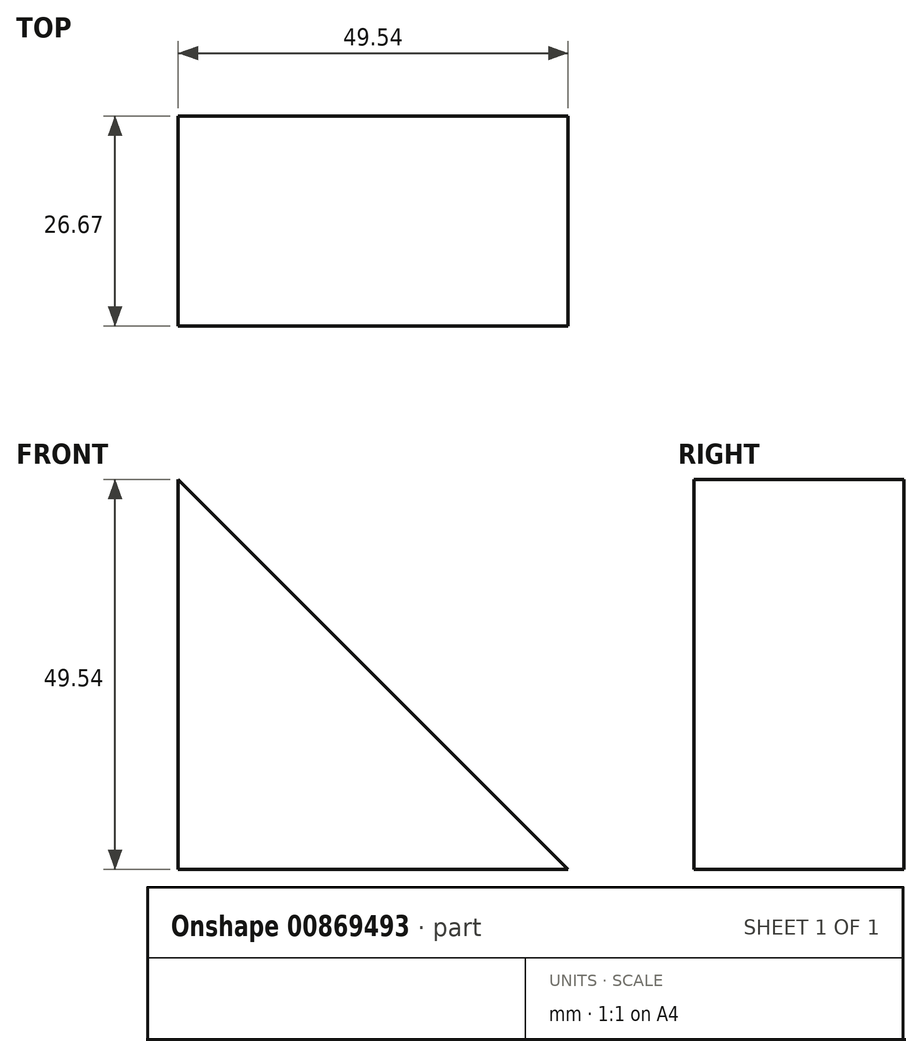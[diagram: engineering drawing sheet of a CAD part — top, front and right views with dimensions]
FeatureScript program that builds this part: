
annotation { "Feature Type Name" : "Feature", "Feature Type Description" : "" }
export const myFeature = defineFeature(function(context is Context, id is Id, definition is map)
    precondition{}
    {
        {
            var Q0;
            Q0=qCreatedBy(makeId("Front.planeOp"),FACE);
            var sketch = newSketch(context, id + "F0", { "sketchPlane" : qUnion([Q0])});
            skLineSegment(sketch, "E0.bottom", {"start": v(24.77, -24.76) * mm, "end": v(-24.76, -24.77) * mm});
            skLineSegment(sketch, "E0.right", {"start": v(-24.77, -24.77) * mm, "end": v(-24.77, 24.77) * mm});
            skPoint(sketch, "E0.middle", {"position": v(0, 0) * mm});
            skPoint(sketch, "E0.left.end.orphan", {"position": v(24.77, 24.77) * mm});
            skLineSegment(sketch, "E1", {"start": v(-24.77, 24.77) * mm, "end": v(24.77, -24.76) * mm});
            skSolve(sketch);
        }
        {
            var Q0;
            Q0 = qSketchRegion(id + "F0", true);
            extrude(context, id + "F1", {"entities" : qUnion([Q0]), "depth" : 26.67 * mm, "offsetDistance" : 25.4 * mm});
        }
    });
